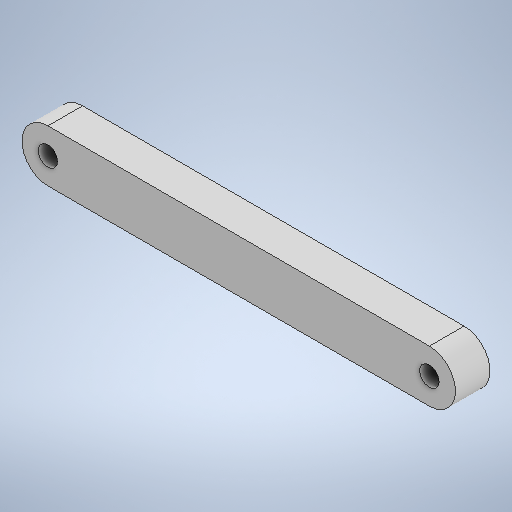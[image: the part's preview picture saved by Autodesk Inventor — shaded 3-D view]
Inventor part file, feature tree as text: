
AUTODESK INVENTOR PART (.ipt)
format: ipt  version: 2025.2 (Build 292293000, 293)  size: 544,256 bytes
history: native  units: in
note: dims shown in document units (in); Inventor stores cm internally (conversion verified against a paired STEP export)
features: extrude x1, sketch x1
ambient origin geometry x8: Origin, YZ Plane, XZ Plane, XY Plane, X Axis, Y Axis, Z Axis, Center Point
bodies: Solid1 (feature_tree)
feature tree (2):
  extrude  "Extrusion1"  Depth=0.1575in TaperAngle=0.0deg
  sketch  "Sketch1"  dims[d0=0.0886in d1=0.0886in d2=0.2362in d3=0.2362in d4=0.1575in d5=0.0in]
